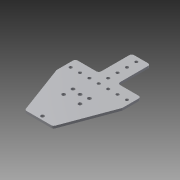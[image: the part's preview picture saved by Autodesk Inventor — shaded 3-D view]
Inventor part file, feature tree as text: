
AUTODESK INVENTOR PART (.ipt)
format: ipt  version: 2014 (Build 180170000, 170)  size: 174,592 bytes
history: native  units: in
note: dims shown in document units (in); Inventor stores cm internally (conversion verified against a paired STEP export)
features: fillet x2, extrude x1, sketch x1
ambient origin geometry x8: Origin, YZ Plane, XZ Plane, XY Plane, X Axis, Y Axis, Z Axis, Center Point
bodies: Solid1 (feature_tree)
feature tree (4):
  extrude  "Extrusion1"  Depth=2.0in
  fillet  "Fillet1"  Radius=0.19in
  fillet  "Fillet2"  Radius=0.19in
  sketch  "Sketch1"  dims[d1=0.19in d2=2.0in d3=0.19in d4=0.19in d5=0.5in d6=0.435in d7=0.435in d9=0.19in d10=0.19in d11=0.435in d12=0.5in d15=0.125in d16=0.0in d22=0.125in d23=0.0625in d24=1.25in d25=1.75in d26=1.0in d28=1.75in d29=1.5in d30=1.5in d31=0.75in d32=2.6875in d33=0.163in d34=0.5in d35=0.25in d36=2.7559in d38=0.5in d39=0.3937in d41=1.0in d43=0.125in d44=0.163in d45=0.25in d46=0.5in d47=1.5748in d49=0.5in d50=0.3937in d52=1.0in d54=0.125in]
